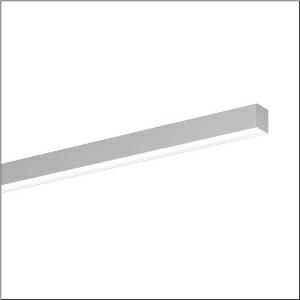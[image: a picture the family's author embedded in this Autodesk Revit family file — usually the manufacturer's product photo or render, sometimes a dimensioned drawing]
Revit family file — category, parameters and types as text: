
# Revit family: silica_21_51mx20da32sb
name_source: partatom
category: Lighting Fixtures
units: mm (PartAtom-declared; Revit-internal decimal feet)

## family parameters
Cut with Voids When Loaded = No
Host = Face
Light Source = No
Part Type = Normal
Room Calculation Point = No
Round Connector Dimension = Use Diameter
Shared = No

## types (1)
- --- (1 x LED, 2400 lm, 16.1 W, 3000K)
    Apparent Load = 16 VA
    CIE Flux Codes = 48 79 96 100 100
    Color Rendering = 80
    Color Temperature = 3000K
    Default Elevation = 1800 mm
    Description = Silica 21, office luminaire, primary optical cover: cover, of PMMA, opal, light emission: direct distribution, primary light characteristic: symmetric, installation type: surface-mounted, LED, rated luminous flux: 2.400lm, luminous efficacy: 149lm/W, light colour: 830, colour temperature: 3000K, control gear: DALI 2, with terminal, 3+2-pole, max. 2.5mm², mains connection: 220..240V, AC, 50/60Hz, rated input power: 16.1W, luminaire housing, of aluminium, metallic grey (RAL 9006), length: 1.204mm, width: 53mm, height: 53mm, protection rating (complete): IP20, insulation class (complete): insulation class I (protective earthing), certification: CE, permissible operating ambient temperature: 0..+35°C, standard: EN 50419, packaging unit: 1 piece
    Height = 53 mm
    Lamp = 1 x LED
    Lamp Light Flux = 2400 lm
    Lamp Power = 16.1 W
    Lamp count = 1
    Length = 1204 mm
    Luminous efficacy = 149 lm/W
    Manufacturer = Siteco
    ModVariant = No
    Model = 51MX20DA32SB
    Mounting Place = Ceiling
    Mounting Type = Surface mounted
    Number of Poles = 1
    OnlyDefault = Yes
    Power Factor = 1
    Product Name = Silica 21
    Product group = office luminaire | ceiling mounted
    ProductGroupID = 301
    Protection Class = Protection class I
    Protection Degree = IP 20
    RLX_Detail_Level = 1
    RLX_Emergency_Light_Flux = 0 lm
    RLX_Emergency_Type = 0
    RLX_Emergency_Type_DB = No
    RlxData = <blob elided: 26141 chars, md5=755ab534>
    Socket = socket
    Standby Power = 0 W
    System Light Flux = 2400 lm
    System Power = 16 W
    Type Comments = factory setting: luminous flux: 100 % | dim-lin: 254 | 233 mA
    Type Image = l_1335933.jpg
    URL = http://relux.com
    VarID = @adj_027753
    Voltage = 0 V
    Weight = 0.00 kg
    Width = 53 mm

## geometry (parser evidence)
native form markers: Blend x4, Sweep x9
no freeform markers — native parametric forms only
